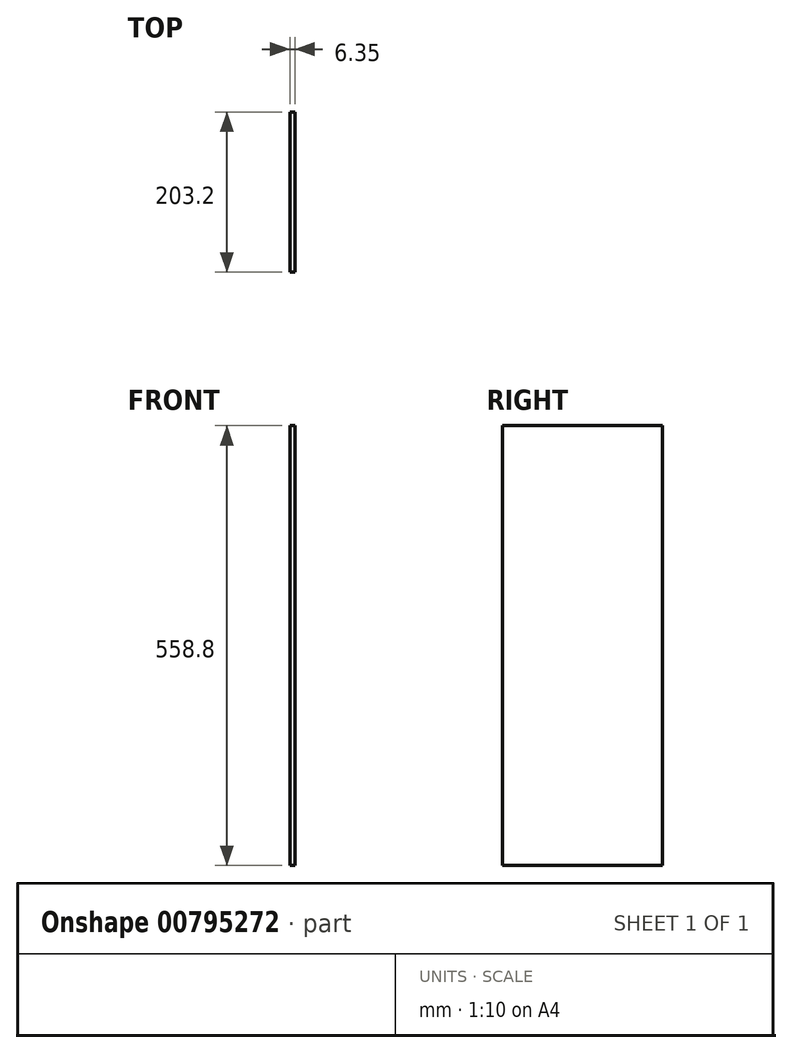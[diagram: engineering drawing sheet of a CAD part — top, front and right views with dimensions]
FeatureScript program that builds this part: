
annotation { "Feature Type Name" : "Feature", "Feature Type Description" : "" }
export const myFeature = defineFeature(function(context is Context, id is Id, definition is map)
    precondition{}
    {
        {
            var Q0;
            Q0=qCreatedBy(makeId("Right.planeOp"),FACE);
            var sketch = newSketch(context, id + "F0", { "sketchPlane" : qUnion([Q0])});
            skLineSegment(sketch, "E0.bottom", {"start": v(101.6, -279.4) * mm, "end": v(-101.6, -279.4) * mm});
            skLineSegment(sketch, "E0.top", {"start": v(101.6, 279.4) * mm, "end": v(-101.6, 279.4) * mm});
            skLineSegment(sketch, "E0.left", {"start": v(101.6, -279.4) * mm, "end": v(101.6, 279.4) * mm});
            skLineSegment(sketch, "E0.right", {"start": v(-101.6, -279.4) * mm, "end": v(-101.6, 279.4) * mm});
            skPoint(sketch, "E0.middle", {"position": v(0, 0) * mm});
            skSolve(sketch);
        }
        {
            var Q0;
            Q0=makeQuery(id+"F0.imprint","IMPRINT",FACE,{"disambiguationData":[TD([[makeQuery(id+"F0.imprint","IMPRINT",EDGE,{"derivedFrom":sQuery(id+"F0.wireOp",EDGE,"E0.bottom")}),-1.0]])]});
            extrude(context, id + "F1", {"entities" : qUnion([Q0]), "depth" : 6.35 * mm, "offsetDistance" : 25.4 * mm});
        }
    });
